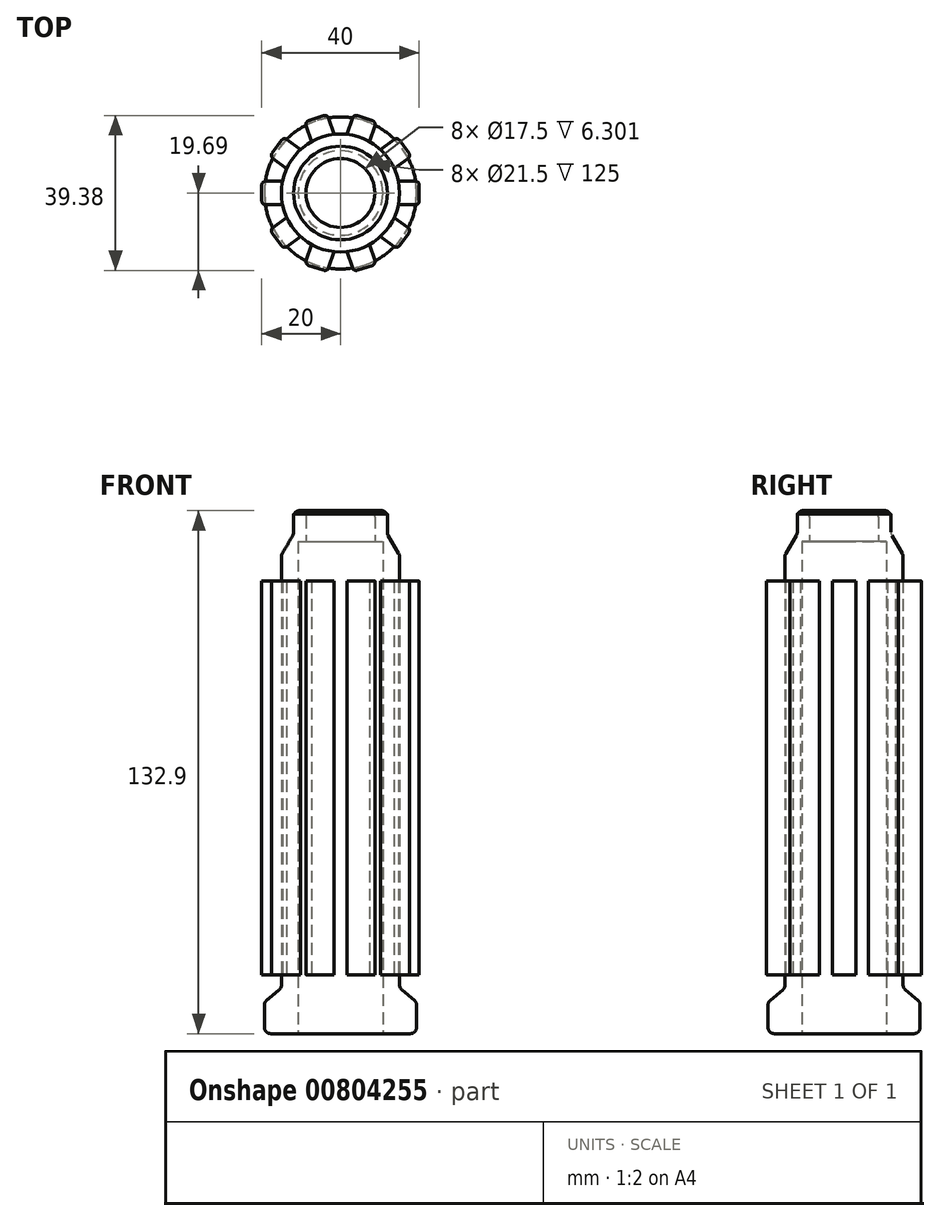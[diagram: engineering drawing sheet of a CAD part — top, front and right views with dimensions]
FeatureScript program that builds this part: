
annotation { "Feature Type Name" : "Feature", "Feature Type Description" : "" }
export const myFeature = defineFeature(function(context is Context, id is Id, definition is map)
    precondition{}
    {
        {
            var Q0;
            Q0=qCreatedBy(makeId("Front.planeOp"),FACE);
            var sketch = newSketch(context, id + "F0", { "sketchPlane" : qUnion([Q0])});
            skLineSegment(sketch, "E0", {"start": v(0, 0) * mm, "end": v(0, 32.06) * mm, "construction": true});
            skLineSegment(sketch, "E1", {"start": v(8.75, 125) * mm, "end": v(8.75, 135) * mm});
            skLineSegment(sketch, "E2", {"start": v(8.75, 125) * mm, "end": v(10.75, 125) * mm});
            skLineSegment(sketch, "E3", {"start": v(10.75, 125) * mm, "end": v(10.75, 0) * mm});
            skLineSegment(sketch, "E4", {"start": v(10.75, 0) * mm, "end": v(19.32, 0) * mm});
            skLineSegment(sketch, "E5", {"start": v(19.32, 0) * mm, "end": v(19.32, 8) * mm});
            skLineSegment(sketch, "E6", {"start": v(19.33, 8) * mm, "end": v(15, 11.63) * mm});
            skLineSegment(sketch, "E7", {"start": v(15, 11.63) * mm, "end": v(15, 121.63) * mm});
            skLineSegment(sketch, "E8", {"start": v(15, 121.63) * mm, "end": v(11.9, 127) * mm});
            skLineSegment(sketch, "E9", {"start": v(11.9, 127) * mm, "end": v(11.9, 132) * mm});
            skArc(sketch, "E10", {"start": v(11.9, 132) * mm, "mid": v(10.36, 133.54) * mm, "end": v(8.75, 135) * mm});
            skSolve(sketch);
        }
        {
            var Q0;
            Q0 = qSketchRegion(id + "F0", true);
            var Q1;
            Q1=sQuery(id+"F0.wireOp",EDGE,"E0");
            revolve(context, id + "F1", {"surfaceOperationType" : NewSurfaceOperationType.NEW, "entities" : qUnion([Q0]), "axis" : qUnion([Q1]), "revolveType" : RevolveType.FULL});
        }
        {
            var Q0;
            Q0=makeQuery(id+"F1.opRevolve","SWEPT_EDGE",EDGE,{"disambiguationData":[OSD([sQuery(id+"F0.wireOp",EDGE,"E1"),sQuery(id+"F0.wireOp",EDGE,"E10")])]});
            var Q1;
            Q1=makeQuery(id+"F1.opRevolve","SWEPT_EDGE",EDGE,{"disambiguationData":[OSD([sQuery(id+"F0.wireOp",EDGE,"E7"),sQuery(id+"F0.wireOp",EDGE,"E8")])]});
            var Q2;
            Q2=makeQuery(id+"F1.opRevolve","SWEPT_EDGE",EDGE,{"disambiguationData":[OSD([sQuery(id+"F0.wireOp",EDGE,"E8"),sQuery(id+"F0.wireOp",EDGE,"E9")])]});
            var Q3;
            Q3=makeQuery(id+"F1.opRevolve","SWEPT_EDGE",EDGE,{"disambiguationData":[OSD([sQuery(id+"F0.wireOp",EDGE,"E6"),sQuery(id+"F0.wireOp",EDGE,"E7")])]});
            var Q4;
            Q4=makeQuery(id+"F1.opRevolve","SWEPT_EDGE",EDGE,{"disambiguationData":[OSD([sQuery(id+"F0.wireOp",EDGE,"E5"),sQuery(id+"F0.wireOp",EDGE,"E6")])]});
            var Q5;
            Q5=makeQuery(id+"F1.opRevolve","SWEPT_EDGE",EDGE,{"disambiguationData":[OSD([sQuery(id+"F0.wireOp",EDGE,"E4"),sQuery(id+"F0.wireOp",EDGE,"E5")])]});
            fillet(context, id + "F2", {"entities" : qUnion([Q0, Q1, Q2, Q3, Q4, Q5]), "radius" : 1.6 * mm, "tangentPropagation" : true, "allowEdgeOverflow" : false});
        }
        {
            var Q0;
            Q0=qCreatedBy(makeId("Right.planeOp"),FACE);
            cPlane(context, id + "F3", {"entities" : qUnion([Q0]), "cplaneType" : CPlaneType.OFFSET, "offset" : 20 * mm, "width" : 150 * mm, "height" : 150 * mm});
        }
        {
            var Q0;
            Q0=qCreatedBy(id+"F3.planeOp",FACE);
            var sketch = newSketch(context, id + "F4", { "sketchPlane" : qUnion([Q0])});
            skLineSegment(sketch, "E11.bottom", {"start": v(-3, 115) * mm, "end": v(3, 115) * mm});
            skLineSegment(sketch, "E11.top", {"start": v(-3, 15) * mm, "end": v(3, 15) * mm});
            skLineSegment(sketch, "E11.left", {"start": v(-3, 115) * mm, "end": v(-3, 15) * mm});
            skLineSegment(sketch, "E11.right", {"start": v(3, 115) * mm, "end": v(3, 15) * mm});
            skSolve(sketch);
        }
        {
            var Q0;
            Q0=makeQuery(id+"F4.imprint","IMPRINT",FACE,{"disambiguationData":[TD([[makeQuery(id+"F4.imprint","IMPRINT",EDGE,{"derivedFrom":sQuery(id+"F4.wireOp",EDGE,"E11.bottom")}),-1.0]])]});
            var Q1;
            Q1=makeQuery(id+"F1.opRevolve","SWEPT_FACE",FACE,{"disambiguationData":[OSD([sQuery(id+"F0.wireOp",EDGE,"E7")])]});
            extrude(context, id + "F5", {"entities" : qUnion([Q0]), "endBound" : BoundingType.UP_TO_SURFACE, "oppositeDirection" : true, "depth" : 25 * mm, "endBoundEntityFace" : qUnion([Q1]), "offsetDistance" : 25 * mm});
        }
        {
            var Q0;
            Q0=makeQuery(id+"F5.opExtrude","CAP_EDGE",EDGE,{"disambiguationData":[OSD([sQuery(id+"F4.wireOp",EDGE,"E11.left")])],"isStart":true});
            var Q1;
            Q1=makeQuery(id+"F5.opExtrude","CAP_EDGE",EDGE,{"disambiguationData":[OSD([sQuery(id+"F4.wireOp",EDGE,"E11.right")])],"isStart":true});
            fillet(context, id + "F6", {"entities" : qUnion([Q0, Q1]), "radius" : 1 * mm, "tangentPropagation" : true, "allowEdgeOverflow" : false});
        }
        {
            var Q0;
            Q0=makeQuery(id+"F5.opExtrude","SWEPT_BODY",BODY,{"disambiguationData":[OSD([sQuery(id+"F4.wireOp",EDGE,"E11.bottom"),sQuery(id+"F4.wireOp",EDGE,"E11.top"),sQuery(id+"F4.wireOp",EDGE,"E11.left"),sQuery(id+"F4.wireOp",EDGE,"E11.right")])]});
            var Q1;
            Q1=makeQuery(id+"F1.opRevolve","SWEPT_FACE",FACE,{"disambiguationData":[OSD([sQuery(id+"F0.wireOp",EDGE,"E7")])]});
            circularPattern(context, id + "F7", {"entities" : qUnion([Q0]), "axis" : qUnion([Q1]), "angle" : 360 * degree, "instanceCount" : 10, "equalSpace" : true});
        }
    });
